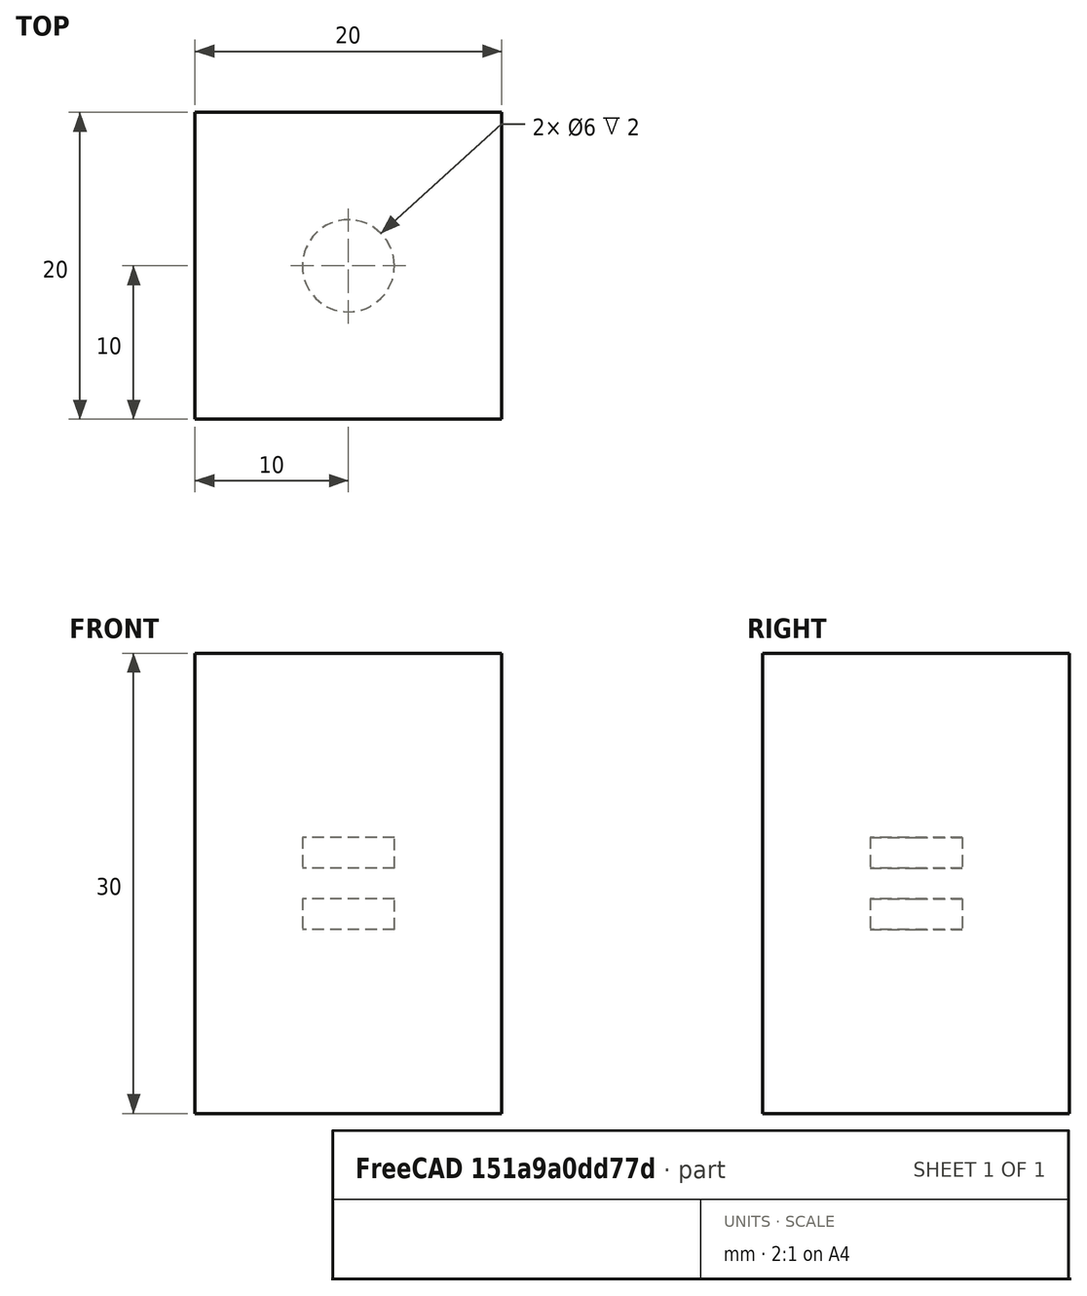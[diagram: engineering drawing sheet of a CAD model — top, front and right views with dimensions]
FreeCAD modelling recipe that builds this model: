
FCSTD DOCUMENT  (FreeCAD 1.0R39109 (Git))
Label: Magnetics-3D
License: All rights reserved
LicenseURL: https://en.wikipedia.org/wiki/All_rights_reserved
objects: PartDesign::Body×3, Sketcher::SketchObject×2, PartDesign::Pad×2, App::MaterialObjectPython×2, App::FeaturePython×1, Fem::FemSolverObjectPython×1, PartDesign::FeatureBase×1, Part::FeaturePython×1, Fem::ConstraintPython×1, Fem::FemMeshShapeBaseObjectPython×1, Fem::FemAnalysis×1
note: 16 computed .brp shape members not serialized (recipe doc carries the construction recipe); baked Part::Feature solids carry a one-line shape summary decoded from their .brp

FEATURE [Sketcher::SketchObject] Sketch
  ArcFitTolerance = 1e-06
  AttachmentSupport = -> [XY_Plane]
  FullyConstrained = true
  MakeInternals = false
  MapMode = 5
  sketch-geometry (1):
    g0: Circle CenterX=0 CenterY=0 CenterZ=0 NormalX=0 NormalY=0 NormalZ=1 AngleXU=0 Radius=3
  constraints (2):
    c: Coincident(g0,g-1)
    c: Diameter(g0) = 6
FEATURE [PartDesign::Pad] Pad
  Direction = (0,0,1)
  Length = 2
  Length2 = 10
  Profile = -> Sketch
  ReferenceAxis = -> Sketch [N_Axis]
  Refine = true
  Suppressed = false
  Type = 0
FEATURE [PartDesign::Body] Body  label="Magnet-1"
  AllowCompound = false
  Group = -> [Sketch,Pad]
  Origin = -> Origin
  Placement = pos=(0,0,1) rot=(0,0,1;0rad)
  Tip = -> Pad
FEATURE [Sketcher::SketchObject] Sketch002
  ArcFitTolerance = 1e-06
  AttachmentSupport = -> [XY_Plane002]
  FullyConstrained = true
  MakeInternals = false
  MapMode = 5
  sketch-geometry (5):
    g0: LineSegment StartX=-10 StartY=-10 StartZ=0 EndX=10 EndY=-10 EndZ=0
    g1: LineSegment StartX=10 StartY=-10 StartZ=0 EndX=10 EndY=10 EndZ=0
    g2: LineSegment StartX=10 StartY=10 StartZ=0 EndX=-10 EndY=10 EndZ=0
    g3: LineSegment StartX=-10 StartY=10 StartZ=0 EndX=-10 EndY=-10 EndZ=0
    g4: GeomPoint [constr] X=0 Y=0 Z=0
  constraints (12):
    c: Coincident(g0,g1)
    c: Coincident(g1,g2)
    c: Coincident(g2,g3)
    c: Coincident(g3,g0)
    c: Horizontal(g0)
    c: Horizontal(g2)
    c: Vertical(g1)
    c: Vertical(g3)
    c: Symmetric(g2,g0,g4)
    c: Distance(g0,g2) = 20
    c: Coincident(g4,g-1)
    c: Equal(g3,g2)
FEATURE [PartDesign::Pad] Pad002
  Direction = (0,0,1)
  Length = 30
  Length2 = 10
  Midplane = true
  Profile = -> Sketch002
  ReferenceAxis = -> Sketch002 [N_Axis]
  Refine = true
  Suppressed = false
  Type = 0
FEATURE [PartDesign::Body] Body002  label="Air"
  AllowCompound = false
  Group = -> [Sketch002,Pad002]
  Origin = -> Origin002
  Tip = -> Pad002
FEATURE [App::FeaturePython] Magnetodynamic  # WARN: FeaturePython — macro-defined, semantics opaque (R4)
  AngularFrequency = 0
  AutomatedSourceProjectionBCs = false
  BiCGstablDegree = 4
  CalculateCurrentDensity = false
  CalculateElectricField = false
  CalculateElementalFields = false
  CalculateHarmonicLoss = false
  CalculateJouleHeating = false
  CalculateMagneticFieldStrength = true
  CalculateMaxwellStress = false
  CalculateNodalFields = true
  CalculateNodalForces = true
  CalculateNodalHeating = false
  DiscontinuousBodies = false
  FixInputCurrentDensity = false
  IdrsParameter = 2
  IsHarmonic = false
  LagrangeGaugePenalizationCoefficient = 0
  LinearDirectMethod = 0
  LinearIterations = 500
  LinearIterativeMethod = 1
  LinearPreconditioning = 0
  LinearSolverType = 1
  LinearSystemRefactorize = false
  LinearSystemSolverDisabled = false
  LinearTolerance = 1e-10
  NonlinearIterations = 20
  NonlinearNewtonAfterIterations = 3
  NonlinearNewtonAfterTolerance = 0.001
  NonlinearTolerance = 1e-07
  Priority = 10
  QuadraticApproximation = false
  RelaxationFactor = 1
  Stabilize = true
  StaticConductivity = false
  SteadyStateTolerance = 1e-05
  UseLagrangeGauge = false
  UsePiolaTransform = false
  UseTreeGauge = false
  expr: LinearTolerance = 1e-10
  expr: NonlinearNewtonAfterTolerance = 0.001
  expr: NonlinearTolerance = 1e-07
  expr: SteadyStateTolerance = 1e-05
FEATURE [Fem::FemSolverObjectPython] SolverElmer  # FEM object (typed FeaturePython)
  BDFOrder = 2
  CoordinateSystem = 0
  Group = -> [Magnetodynamic]
  OutputIntervals = [1]
  SimulationType = 1
  SteadyStateMaxIterations = 1
  SteadyStateMinIterations = 0
  TimestepIntervals = [100]
  TimestepSizes = [0.1]
FEATURE [PartDesign::FeatureBase] Clone
  BaseFeature = -> Body
  Placement = pos=(0,0,1) rot=(0,0,1;0rad)
  Suppressed = false
FEATURE [App::MaterialObjectPython] MaterialSolid  # material (typed FeaturePython)
  Category = 0
  Material = AmbientColor=(0.0020, 0.0020, 0.0020, 1.0); Author=Uwe Stöhr; CardName=Iron-Generic; Density=7.874e-06 kg/mm^3; DiffuseColor=(0.0000, 0.0000, 0.0000, 1.0); ElectricalConductivity=0.0103 s^3*A^2/(mm^3*kg); EmissiveColor=(0.0000, 0.0000, 0.0000, 1.0); Father=Metal; KindOfMaterial=Iron; Name=Iron-Generic; PoissonRatio=0.29; RelativePermeability=5000; ShearModulus=8.2e+07 kg/(mm*s^2); Shininess=0.06; SpecificHeat=4.605e+08 mm^2/(s^2*K); SpecularColor=(0.9800, 0.9800, 0.9800, 1.0); ThermalConductivity=80400 mm*kg/(s^3*K); ThermalExpansionCoefficient=1.18e-05 1/K; Transparency=0; UltimateTensileStrength=497000 kg/(mm*s^2); YieldStrength=428000 kg/(mm*s^2); YoungsModulus=2.11e+08 kg/(mm*s^2)
  References = -> [Pad,Clone]
  UUID = 1826c364-d26a-43fb-8f61-288281236836
FEATURE [PartDesign::Body] Body003  label="Magnet-2"
  AllowCompound = false
  Group = -> [Clone]
  Origin = -> Origin003
  Placement = pos=(0,0,-4) rot=(0,0,1;0rad)
  Tip = -> Clone
FEATURE [Part::FeaturePython] BooleanFragments  # WARN: FeaturePython — macro-defined, semantics opaque (R4)
  Mode = 0
  Objects = -> [Body,Body002,Body003]
  Tolerance = 0
FEATURE [Fem::ConstraintPython] ConstraintMagnetization  label="MagnetizationMagnet"  # FEM object (typed FeaturePython)
  Magnetization_im_1 = 0
  Magnetization_im_1_Disabled = true
  Magnetization_im_2 = 0
  Magnetization_im_2_Disabled = true
  Magnetization_im_3 = 0
  Magnetization_im_3_Disabled = true
  Magnetization_re_1 = 0
  Magnetization_re_1_Disabled = true
  Magnetization_re_2 = 0
  Magnetization_re_2_Disabled = true
  Magnetization_re_3 = 5
  Magnetization_re_3_Disabled = false
  NormalDirection = (0,0,1)
  References = -> [Pad,BooleanFragments]
  Suppressed = false
FEATURE [Fem::FemMeshShapeBaseObjectPython] FEMMeshGmsh  # FEM object (typed FeaturePython)
  Algorithm2D = 0
  Algorithm3D = 0
  CharacteristicLengthMax = 1
  CharacteristicLengthMin = 0.1
  CoherenceMesh = true
  ElementDimension = 0
  ElementOrder = 0
  GeometryTolerance = 1e-06
  GroupsOfNodes = false
  HighOrderOptimize = 0
  MeshSizeFromCurvature = 12
  OptimizeNetgen = false
  OptimizeStd = true
  RecombinationAlgorithm = 0
  Recombine3DAll = false
  RecombineAll = false
  SecondOrderLinear = true
  Shape = -> BooleanFragments
  SubdivisionAlgorithm = 0
FEATURE [App::MaterialObjectPython] MaterialFluid  # material (typed FeaturePython)
  Category = 1
  Material = AuthorAndLicense=GPL-2.0-or-later; CardName=Air; Density=1.204e-09 kg/mm^3; Description=Dry air properties at 20 Degrees Celsius and 1 atm; DynamicViscosity=1.8e-08 kg/(mm*s); ElectricalConductivity=1e-21 s^3*A^2/(mm^3*kg); Father=Gas; KinematicViscosity=15.11 mm^2/s; License=GPL-2.0-or-later; Name=Air; PrandtlNumber=0.7; RelativePermeability=1; RelativePermittivity=1.00059; SpecificHeat=1.01e+09 mm^2/(s^2*K); ThermalConductivity=25.87 mm*kg/(s^3*K); ThermalExpansionCoefficient=0.00343 1/K
  References = -> [BooleanFragments]
  UUID = 94370b96-c97e-4a3f-83b2-11d7461f7da7
FEATURE [Fem::FemAnalysis] Analysis
  Group = -> [SolverElmer,MaterialSolid,ConstraintMagnetization,FEMMeshGmsh,MaterialFluid]
